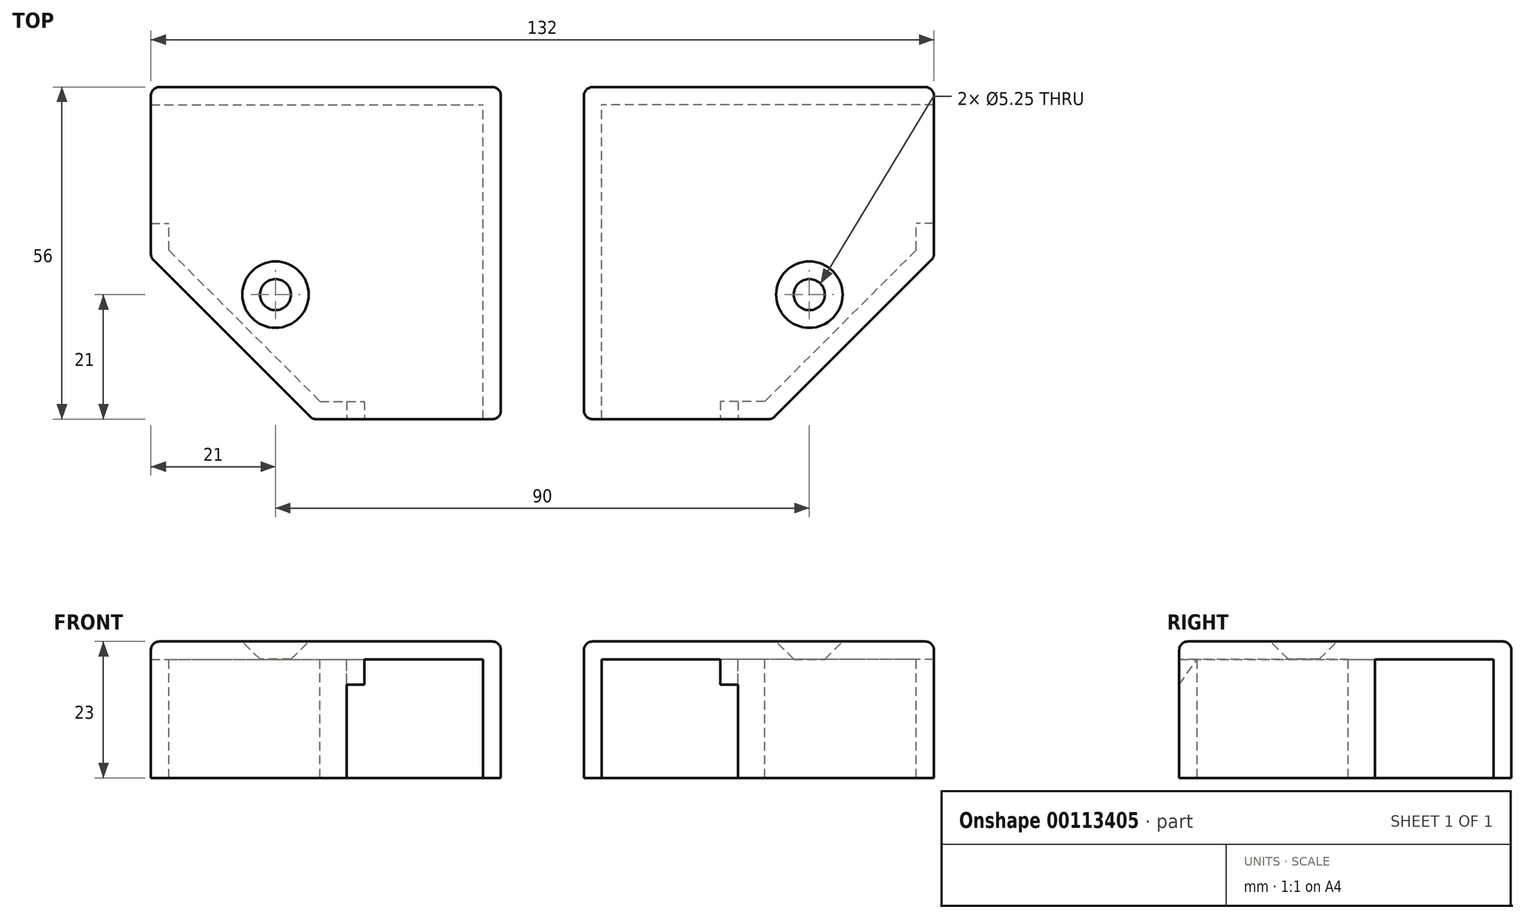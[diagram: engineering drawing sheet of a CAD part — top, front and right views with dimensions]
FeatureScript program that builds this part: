
annotation { "Feature Type Name" : "Feature", "Feature Type Description" : "" }
export const myFeature = defineFeature(function(context is Context, id is Id, definition is map)
    precondition{}
    {
        {
            var Q0;
            Q0=qCreatedBy(makeId("Top.planeOp"),FACE);
            var sketch = newSketch(context, id + "F0", { "sketchPlane" : qUnion([Q0])});
            skLineSegment(sketch, "E0", {"start": v(0, 0) * mm, "end": v(0, -100) * mm, "construction": true});
            skLineSegment(sketch, "E1", {"start": v(0, 0) * mm, "end": v(-100, 0) * mm, "construction": true});
            skLineSegment(sketch, "E2", {"start": v(0, -20) * mm, "end": v(-100, -20) * mm, "construction": true});
            skLineSegment(sketch, "E3", {"start": v(-20, 0) * mm, "end": v(-20, -100) * mm, "construction": true});
            skLineSegment(sketch, "E4", {"start": v(-53, -20) * mm, "end": v(-53, -24.5) * mm, "construction": true});
            skLineSegment(sketch, "E5", {"start": v(-53, -24.5) * mm, "end": v(-27.5, -50) * mm, "construction": true});
            skLineSegment(sketch, "E6", {"start": v(-27.5, -50) * mm, "end": v(-20, -50) * mm, "construction": true});
            skPoint(sketch, "E7", {"position": v(-35, -32) * mm});
            skLineSegment(sketch, "E8", {"start": v(-23, -20) * mm, "end": v(-23, -50) * mm, "construction": true});
            skLineSegment(sketch, "E9", {"start": v(-56, 3) * mm, "end": v(3, 3) * mm});
            skLineSegment(sketch, "E10", {"start": v(3, 3) * mm, "end": v(3, -53) * mm});
            skLineSegment(sketch, "E11", {"start": v(3, -53) * mm, "end": v(-28.74, -53) * mm});
            skLineSegment(sketch, "E12", {"start": v(-28.74, -53) * mm, "end": v(-56, -25.74) * mm});
            skLineSegment(sketch, "E13", {"start": v(-56, -25.74) * mm, "end": v(-56, 3) * mm});
            skLineSegment(sketch, "E14", {"start": v(0, -53) * mm, "end": v(0, 0) * mm});
            skLineSegment(sketch, "E15", {"start": v(-56, -20) * mm, "end": v(-53, -20) * mm});
            skLineSegment(sketch, "E16", {"start": v(-53, -24.5) * mm, "end": v(-27.5, -50) * mm});
            skLineSegment(sketch, "E17", {"start": v(-20, -50) * mm, "end": v(-20, -53) * mm});
            skLineSegment(sketch, "E18", {"start": v(-53, -24.5) * mm, "end": v(-53, -20) * mm});
            skLineSegment(sketch, "E19", {"start": v(-27.5, -50) * mm, "end": v(-20, -50) * mm});
            skLineSegment(sketch, "E20", {"start": v(-56, 0) * mm, "end": v(0, 0) * mm});
            skSolve(sketch);
        }
        {
            var Q0;
            Q0 = qSketchRegion(id + "F0", true);
            extrude(context, id + "F1", {"entities" : qUnion([Q0]), "depth" : 3 * mm});
        }
        {
            var Q0;
            {var subQ1=sQuery(id+"F0.wireOp",EDGE,"E9");Q0=makeQuery(id+"F0.imprint","IMPRINT",FACE,{"disambiguationData":[TD([[makeQuery(id+"F0.imprint","IMPRINT",EDGE,{"derivedFrom":subQ1}),-1.0]])]});}
            var Q1;
            {var subQ2=sQuery(id+"F0.wireOp",EDGE,"E12");Q1=makeQuery(id+"F0.imprint","IMPRINT",FACE,{"disambiguationData":[TD([[makeQuery(id+"F0.imprint","IMPRINT",EDGE,{"derivedFrom":subQ2}),-1.0]])]});}
            extrude(context, id + "F2", {"entities" : qUnion([Q0, Q1]), "operationType" : NewBodyOperationType.ADD, "oppositeDirection" : true, "depth" : 20 * mm});
        }
        {
            var Q0;
            {var subQ0=sQuery(id+"F0.wireOp",EDGE,"E10");var subQ1=sQuery(id+"F0.wireOp",EDGE,"E9");Q0=makeQuery(id+"F2.boolean.opBoolean","MERGE",EDGE,{"derivedFrom":[makeQuery(id+"F1.opExtrude","SWEPT_EDGE",EDGE,{"disambiguationData":[OSD([subQ1,subQ0])]}),makeQuery(id+"F2.opExtrude","SWEPT_EDGE",EDGE,{"disambiguationData":[OSD([subQ1,subQ0])]})]});}
            var Q1;
            Q1=makeQuery(id+"F1.opExtrude","CAP_EDGE",EDGE,{"disambiguationData":[OSD([sQuery(id+"F0.wireOp",EDGE,"E10")])],"isStart":false});
            var Q2;
            Q2=makeQuery(id+"F1.opExtrude","CAP_EDGE",EDGE,{"disambiguationData":[OSD([sQuery(id+"F0.wireOp",EDGE,"E9")])],"isStart":false});
            var Q3;
            Q3=makeQuery(id+"F1.opExtrude","CAP_EDGE",EDGE,{"disambiguationData":[OSD([sQuery(id+"F0.wireOp",EDGE,"E12")])],"isStart":false});
            var Q4;
            {var subQ0=sQuery(id+"F0.wireOp",EDGE,"E12");var subQ1=sQuery(id+"F0.wireOp",EDGE,"E11");Q4=makeQuery(id+"F2.boolean.opBoolean","MERGE",EDGE,{"derivedFrom":[makeQuery(id+"F1.opExtrude","SWEPT_EDGE",EDGE,{"disambiguationData":[OSD([subQ1,subQ0])]}),makeQuery(id+"F2.opExtrude","SWEPT_EDGE",EDGE,{"disambiguationData":[OSD([subQ1,subQ0])]})]});}
            var Q5;
            {var subQ0=sQuery(id+"F0.wireOp",EDGE,"E13");var subQ1=sQuery(id+"F0.wireOp",EDGE,"E12");Q5=makeQuery(id+"F2.boolean.opBoolean","MERGE",EDGE,{"derivedFrom":[makeQuery(id+"F1.opExtrude","SWEPT_EDGE",EDGE,{"disambiguationData":[OSD([subQ1,subQ0])]}),makeQuery(id+"F2.opExtrude","SWEPT_EDGE",EDGE,{"disambiguationData":[OSD([subQ1,subQ0])]})]});}
            var Q6;
            {var subQ0=sQuery(id+"F0.wireOp",EDGE,"E11");var subQ1=sQuery(id+"F0.wireOp",EDGE,"E10");Q6=makeQuery(id+"F2.boolean.opBoolean","MERGE",EDGE,{"derivedFrom":[makeQuery(id+"F1.opExtrude","SWEPT_EDGE",EDGE,{"disambiguationData":[OSD([subQ1,subQ0])]}),makeQuery(id+"F2.opExtrude","SWEPT_EDGE",EDGE,{"disambiguationData":[OSD([subQ1,subQ0])]})]});}
            var Q7;
            {var subQ0=sQuery(id+"F0.wireOp",EDGE,"E13");var subQ1=sQuery(id+"F0.wireOp",EDGE,"E9");Q7=makeQuery(id+"F2.boolean.opBoolean","MERGE",EDGE,{"derivedFrom":[makeQuery(id+"F1.opExtrude","SWEPT_EDGE",EDGE,{"disambiguationData":[OSD([subQ1,subQ0])]}),makeQuery(id+"F2.opExtrude","SWEPT_EDGE",EDGE,{"disambiguationData":[OSD([subQ1,subQ0])]})]});}
            var Q8;
            Q8=makeQuery(id+"F1.opExtrude","CAP_EDGE",EDGE,{"disambiguationData":[OSD([sQuery(id+"F0.wireOp",EDGE,"E13")])],"isStart":false});
            var Q9;
            Q9=makeQuery(id+"F1.opExtrude","CAP_EDGE",EDGE,{"disambiguationData":[OSD([sQuery(id+"F0.wireOp",EDGE,"E11")])],"isStart":false});
            fillet(context, id + "F3", {"entities" : qUnion([Q0, Q1, Q2, Q3, Q4, Q5, Q6, Q7, Q8, Q9]), "radius" : 1.44 * mm, "tangentPropagation" : true, "allowEdgeOverflow" : false});
        }
        {
            var Q0;
            Q0=makeQuery(id+"F1.opExtrude","CAP_FACE",FACE,{"disambiguationData":[OSD([sQuery(id+"F0.wireOp",EDGE,"E9"),sQuery(id+"F0.wireOp",EDGE,"E10"),sQuery(id+"F0.wireOp",EDGE,"E11"),sQuery(id+"F0.wireOp",EDGE,"E12"),sQuery(id+"F0.wireOp",EDGE,"E13")])],"isStart":false});
            var sketch = newSketch(context, id + "F4", { "sketchPlane" : qUnion([Q0])});
            skPoint(sketch, "E21.0", {"position": v(-35, -32) * mm});
            skSolve(sketch);
        }
        {
            var Q0;
            Q0=sQuery(id+"F4.wireOp",VERTEX,"E21.0");
            var Q1;
            Q1=makeQuery(id+"F1.opExtrude","SWEPT_BODY",BODY,{"disambiguationData":[OSD([sQuery(id+"F0.wireOp",EDGE,"E9"),sQuery(id+"F0.wireOp",EDGE,"E10"),sQuery(id+"F0.wireOp",EDGE,"E11"),sQuery(id+"F0.wireOp",EDGE,"E12"),sQuery(id+"F0.wireOp",EDGE,"E13")])]});
            hole(context, id + "F5", {"style" : HoleStyle.C_SINK, "endStyle" : HoleEndStyle.BLIND, "standardTappedOrClearance" : lookupTablePath({ "standard" : "ISO", "fit" : "Close", "size" : "M5", "type" : "Clearance" }), "standardBlindInLast" : lookupTablePath({ "fit" : "Close", "standard" : "ISO", "size" : "M5", "type" : "Clearance" }), "holeDiameter" : 5.25 * mm, "cSinkDiameter" : 11.2 * mm, "cSinkAngle" : 90 * degree, "holeDepth" : 6 * mm, "startFromSketch" : true, "locations" : qUnion([Q0]), "scope" : qUnion([Q1])});
        }
        {
            var Q0;
            Q0=qCreatedBy(makeId("Right.planeOp"),FACE);
            cPlane(context, id + "F6", {"entities" : qUnion([Q0]), "cplaneType" : CPlaneType.OFFSET, "offset" : 10 * mm, "width" : 150 * mm, "height" : 150 * mm});
        }
        {
            var Q0;
            Q0=makeQuery(id+"F2.opExtrude","SWEPT_FACE",FACE,{"disambiguationData":[OSD([sQuery(id+"F0.wireOp",EDGE,"E17")])]});
            var sketch = newSketch(context, id + "F7", { "sketchPlane" : qUnion([Q0])});
            skLineSegment(sketch, "E22", {"start": v(-50, 0) * mm, "end": v(-50, -20) * mm});
            skLineSegment(sketch, "E23", {"start": v(-50, -20) * mm, "end": v(-64, -20) * mm});
            skLineSegment(sketch, "E24", {"start": v(-64, -20) * mm, "end": v(-50, 0) * mm});
            skSolve(sketch);
        }
        {
            var Q0;
            Q0 = qSketchRegion(id + "F7", true);
            extrude(context, id + "F8", {"entities" : qUnion([Q0]), "operationType" : NewBodyOperationType.REMOVE, "oppositeDirection" : true, "depth" : 3 * mm});
        }
        {
            var Q0;
            Q0=makeQuery(id+"F1.opExtrude","SWEPT_BODY",BODY,{"disambiguationData":[OSD([sQuery(id+"F0.wireOp",EDGE,"E9"),sQuery(id+"F0.wireOp",EDGE,"E10"),sQuery(id+"F0.wireOp",EDGE,"E11"),sQuery(id+"F0.wireOp",EDGE,"E12"),sQuery(id+"F0.wireOp",EDGE,"E13")])]});
            var Q1;
            Q1=qCreatedBy(id+"F6.planeOp",FACE);
            mirror(context, id + "F9", {"entities" : qUnion([Q0]), "mirrorPlane" : qUnion([Q1])});
        }
    });
